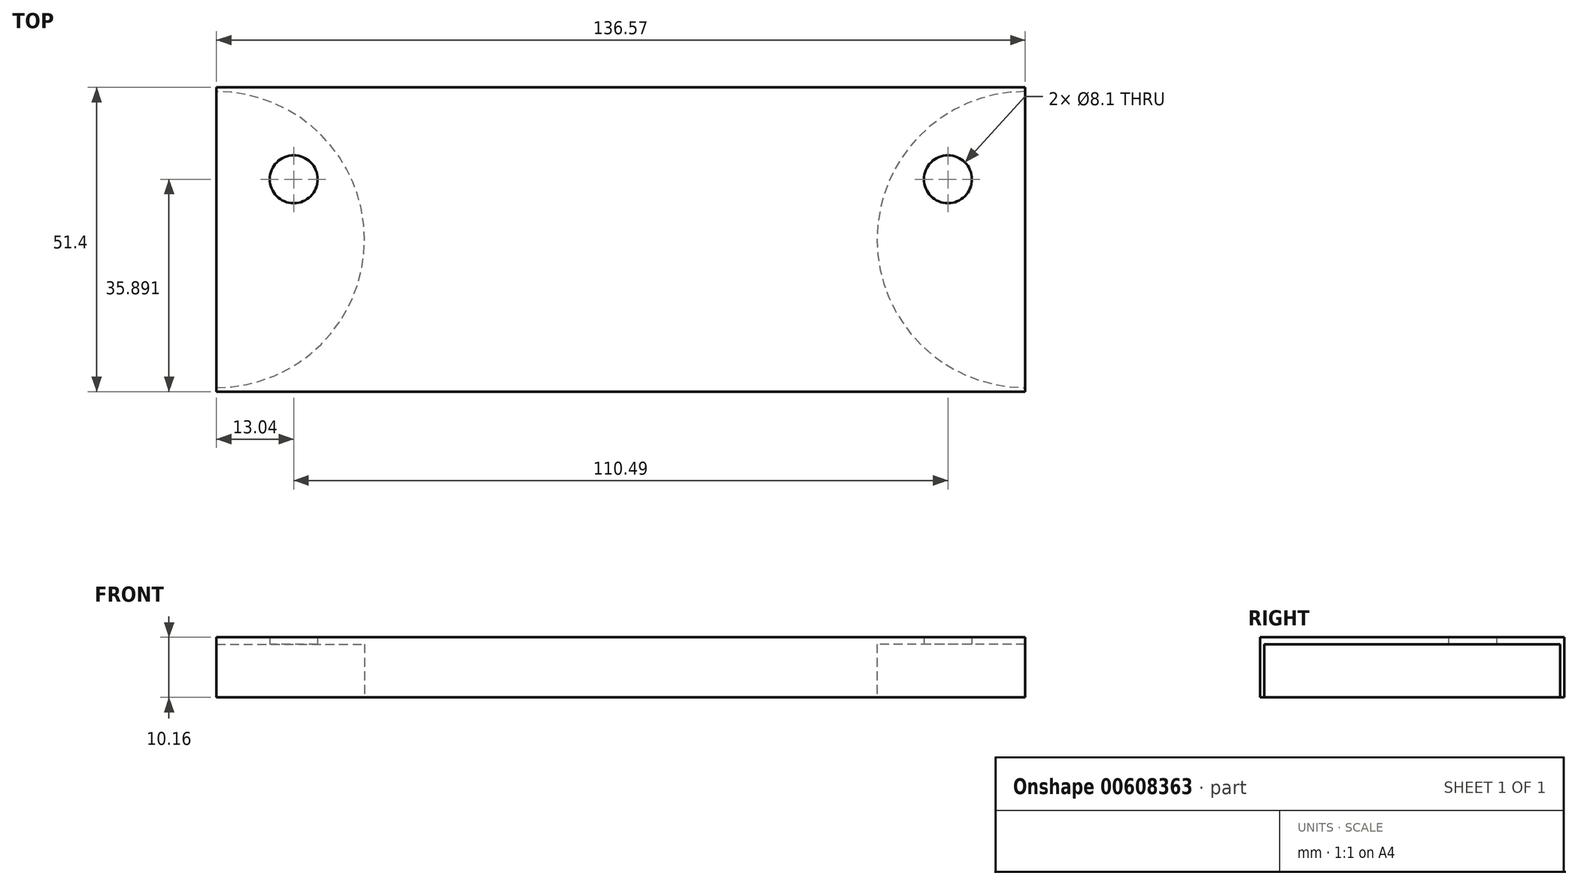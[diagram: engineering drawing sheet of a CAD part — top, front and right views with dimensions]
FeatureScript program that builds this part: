
annotation { "Feature Type Name" : "Feature", "Feature Type Description" : "" }
export const myFeature = defineFeature(function(context is Context, id is Id, definition is map)
    precondition{}
    {
        {
            var Q0;
            Q0=qCreatedBy(makeId("Top.planeOp"),FACE);
            var sketch = newSketch(context, id + "F0", { "sketchPlane" : qUnion([Q0])});
            skCircle(sketch, "E0", {"center": v(0, 0) * mm, "radius": 25.7 * mm});
            skCircle(sketch, "E1", {"center": v(13.04, 10.2) * mm, "radius": 4.05 * mm});
            skLineSegment(sketch, "E2", {"start": v(16.23, 12.69) * mm, "end": v(20.25, 15.83) * mm, "construction": true});
            skCircle(sketch, "E3", {"center": v(136.57, 0) * mm, "radius": 25.7 * mm});
            skCircle(sketch, "E4", {"center": v(123.53, 10.2) * mm, "radius": 4.05 * mm});
            skLineSegment(sketch, "E5", {"start": v(120.34, 12.69) * mm, "end": v(116.32, 15.83) * mm, "construction": true});
            skLineSegment(sketch, "E6", {"start": v(17.1, 10.2) * mm, "end": v(119.48, 10.2) * mm, "construction": true});
            skLineSegment(sketch, "E7", {"start": v(25.7, 0) * mm, "end": v(110.87, 0) * mm, "construction": true});
            skCircle(sketch, "E8", {"center": v(0, 0) * mm, "radius": 25 * mm});
            skCircle(sketch, "E9", {"center": v(136.57, 0) * mm, "radius": 25 * mm});
            skSolve(sketch);
        }
        {
            var Q0;
            Q0=makeQuery(id+"F0.imprint","IMPRINT",FACE,{"disambiguationData":[TD([[makeQuery(id+"F0.imprint","IMPRINT",EDGE,{"derivedFrom":sQuery(id+"F0.wireOp",EDGE,"E0")}),1.0]])]});
            var Q1;
            Q1=makeQuery(id+"F0.imprint","IMPRINT",FACE,{"disambiguationData":[TD([[makeQuery(id+"F0.imprint","IMPRINT",EDGE,{"derivedFrom":sQuery(id+"F0.wireOp",EDGE,"E1")}),-1.0]])]});
            var Q2;
            Q2=makeQuery(id+"F0.imprint","IMPRINT",FACE,{"disambiguationData":[TD([[makeQuery(id+"F0.imprint","IMPRINT",EDGE,{"derivedFrom":sQuery(id+"F0.wireOp",EDGE,"E3")}),1.0]])]});
            var Q3;
            Q3=makeQuery(id+"F0.imprint","IMPRINT",FACE,{"disambiguationData":[TD([[makeQuery(id+"F0.imprint","IMPRINT",EDGE,{"derivedFrom":sQuery(id+"F0.wireOp",EDGE,"E4")}),-1.0]])]});
            extrude(context, id + "F1", {"entities" : qUnion([Q0, Q1, Q2, Q3]), "depth" : 9.16 * mm, "offsetDistance" : 25 * mm});
        }
        {
            var Q0;
            Q0=qCreatedBy(makeId("Top.planeOp"),FACE);
            var sketch = newSketch(context, id + "F2", { "sketchPlane" : qUnion([Q0])});
            skCircle(sketch, "E10", {"center": v(13.04, 10.2) * mm, "radius": 4.05 * mm});
            skLineSegment(sketch, "E11", {"start": v(16.23, 12.69) * mm, "end": v(20.25, 15.83) * mm, "construction": true});
            skCircle(sketch, "E12", {"center": v(123.53, 10.2) * mm, "radius": 4.05 * mm});
            skLineSegment(sketch, "E13", {"start": v(120.34, 12.69) * mm, "end": v(116.32, 15.83) * mm, "construction": true});
            skLineSegment(sketch, "E14", {"start": v(17.1, 10.2) * mm, "end": v(119.48, 10.2) * mm, "construction": true});
            skCircle(sketch, "E15", {"center": v(0, 0) * mm, "radius": 25 * mm});
            skCircle(sketch, "E16", {"center": v(136.57, 0) * mm, "radius": 25 * mm});
            skSolve(sketch);
        }
        {
            var Q0;
            Q0=qCreatedBy(makeId("Top.planeOp"),FACE);
            var sketch = newSketch(context, id + "F3", { "sketchPlane" : qUnion([Q0])});
            skLineSegment(sketch, "E17.bottom", {"start": v(0, 25.7) * mm, "end": v(136.57, 25.7) * mm});
            skLineSegment(sketch, "E17.top", {"start": v(0, -25.7) * mm, "end": v(136.57, -25.7) * mm});
            skLineSegment(sketch, "E17.left", {"start": v(0, 25.7) * mm, "end": v(0, -25.7) * mm});
            skLineSegment(sketch, "E17.right", {"start": v(136.57, 25.7) * mm, "end": v(136.57, -25.7) * mm});
            skPoint(sketch, "E18.endSnap0", {"position": v(136.57, 0) * mm});
            skLineSegment(sketch, "E19", {"start": v(162.27, 0) * mm, "end": v(110.87, 0) * mm, "construction": true});
            skSolve(sketch);
        }
        {
            var Q0;
            Q0=qSketchRegion(id+"F3",true);
            extrude(context, id + "F4", {"entities" : qUnion([Q0]), "operationType" : NewBodyOperationType.ADD, "depth" : 9.16 * mm, "offsetDistance" : 25 * mm});
        }
        {
            var Q0;
            Q0=qSketchRegion(id+"F2",true);
            extrude(context, id + "F5", {"entities" : qUnion([Q0]), "operationType" : NewBodyOperationType.REMOVE, "depth" : 9 * mm, "offsetDistance" : 25 * mm});
        }
        {
            var Q0;
            Q0=makeQuery(id+"F5.boolean.opBoolean","SPLIT",FACE,{"disambiguationData":[TD([makeQuery(id+"F5.opExtrude","SWEPT_FACE",FACE,{"disambiguationData":[OSD([sQuery(id+"F2.wireOp",EDGE,"E12")])]})])],"derivedFrom":makeQuery(id+"F4.boolean.opBoolean","MERGE",FACE,{"derivedFrom":[makeQuery(id+"F1.opExtrude","CAP_FACE",FACE,{"disambiguationData":[OSD([sQuery(id+"F0.wireOp",EDGE,"E0"),sQuery(id+"F0.wireOp",EDGE,"E1")])],"isStart":true}),makeQuery(id+"F1.opExtrude","CAP_FACE",FACE,{"disambiguationData":[OSD([sQuery(id+"F0.wireOp",EDGE,"E3"),sQuery(id+"F0.wireOp",EDGE,"E4")])],"isStart":true}),makeQuery(id+"F4.opExtrude","CAP_FACE",FACE,{"disambiguationData":[OSD([sQuery(id+"F3.wireOp",EDGE,"E17.bottom"),sQuery(id+"F3.wireOp",EDGE,"E17.top"),sQuery(id+"F3.wireOp",EDGE,"E17.left"),sQuery(id+"F3.wireOp",EDGE,"E17.right")])],"isStart":true})]})});
            var Q1;
            Q1=makeQuery(id+"F5.boolean.opBoolean","SPLIT",FACE,{"disambiguationData":[TD([makeQuery(id+"F5.opExtrude","SWEPT_FACE",FACE,{"disambiguationData":[OSD([sQuery(id+"F2.wireOp",EDGE,"E10")])]})])],"derivedFrom":makeQuery(id+"F4.boolean.opBoolean","MERGE",FACE,{"derivedFrom":[makeQuery(id+"F1.opExtrude","CAP_FACE",FACE,{"disambiguationData":[OSD([sQuery(id+"F0.wireOp",EDGE,"E0"),sQuery(id+"F0.wireOp",EDGE,"E1")])],"isStart":true}),makeQuery(id+"F1.opExtrude","CAP_FACE",FACE,{"disambiguationData":[OSD([sQuery(id+"F0.wireOp",EDGE,"E3"),sQuery(id+"F0.wireOp",EDGE,"E4")])],"isStart":true}),makeQuery(id+"F4.opExtrude","CAP_FACE",FACE,{"disambiguationData":[OSD([sQuery(id+"F3.wireOp",EDGE,"E17.bottom"),sQuery(id+"F3.wireOp",EDGE,"E17.top"),sQuery(id+"F3.wireOp",EDGE,"E17.left"),sQuery(id+"F3.wireOp",EDGE,"E17.right")])],"isStart":true})]})});
            var Q2;
            Q2=sQuery(id+"F2.wireOp",EDGE,"E12");
            var Q3;
            Q3=sQuery(id+"F2.wireOp",EDGE,"E10");
            extrude(context, id + "F6", {"entities" : qUnion([Q0, Q1]), "operationType" : NewBodyOperationType.REMOVE, "surfaceEntities" : qUnion([Q2, Q3]), "oppositeDirection" : true, "depth" : 25 * mm, "offsetDistance" : 25 * mm});
        }
        {
            var Q0;
            Q0=qCreatedBy(makeId("Top.planeOp"),FACE);
            var sketch = newSketch(context, id + "F7", { "sketchPlane" : qUnion([Q0])});
            skLineSegment(sketch, "E20.left", {"start": v(162.27, 0) * mm, "end": v(162.27, 37.04) * mm, "construction": true});
            skLineSegment(sketch, "E20.right", {"start": v(-25.7, 0) * mm, "end": v(-25.7, 37.04) * mm, "construction": true});
            skLineSegment(sketch, "E21.left", {"start": v(162.27, 0) * mm, "end": v(162.27, -37.04) * mm, "construction": true});
            skLineSegment(sketch, "E21.right", {"start": v(-25.7, 0) * mm, "end": v(-25.7, -37.04) * mm, "construction": true});
            skLineSegment(sketch, "E22.bottom", {"start": v(162.27, 37.04) * mm, "end": v(136.57, 37.04) * mm});
            skLineSegment(sketch, "E22.top", {"start": v(162.27, -37.04) * mm, "end": v(136.57, -37.04) * mm});
            skLineSegment(sketch, "E22.left", {"start": v(162.27, 37.04) * mm, "end": v(162.27, -37.04) * mm});
            skLineSegment(sketch, "E22.right", {"start": v(136.57, 37.04) * mm, "end": v(136.57, -37.04) * mm});
            skLineSegment(sketch, "E23.bottom", {"start": v(-25.7, 37.04) * mm, "end": v(0, 37.04) * mm});
            skLineSegment(sketch, "E23.top", {"start": v(-25.7, -37.04) * mm, "end": v(0, -37.04) * mm});
            skLineSegment(sketch, "E23.left", {"start": v(-25.7, 37.04) * mm, "end": v(-25.7, -37.04) * mm});
            skLineSegment(sketch, "E23.right", {"start": v(0, 37.04) * mm, "end": v(0, -37.04) * mm});
            skLineSegment(sketch, "E24", {"start": v(162.27, 0) * mm, "end": v(-25.7, 0) * mm, "construction": true});
            skLineSegment(sketch, "E25", {"start": v(136.57, -25) * mm, "end": v(136.57, 25) * mm, "construction": true});
            skPoint(sketch, "E26", {"position": v(136.57, 0) * mm});
            skSolve(sketch);
        }
        {
            var Q0;
            Q0=makeQuery(id+"F7.imprint","IMPRINT",FACE,{"disambiguationData":[TD([[makeQuery(id+"F7.imprint","IMPRINT",EDGE,{"derivedFrom":sQuery(id+"F7.wireOp",EDGE,"E23.bottom")}),-1.0]])]});
            var Q1;
            Q1=makeQuery(id+"F7.imprint","IMPRINT",FACE,{"disambiguationData":[TD([[makeQuery(id+"F7.imprint","IMPRINT",EDGE,{"derivedFrom":sQuery(id+"F7.wireOp",EDGE,"E22.bottom")}),1.0]])]});
            extrude(context, id + "F8", {"entities" : qUnion([Q0, Q1]), "operationType" : NewBodyOperationType.REMOVE, "depth" : 25 * mm, "offsetDistance" : 25 * mm});
        }
        {
            var Q0;
            Q0=makeQuery(id+"F4.boolean.opBoolean","MERGE",FACE,{"derivedFrom":[makeQuery(id+"F1.opExtrude","CAP_FACE",FACE,{"disambiguationData":[OSD([sQuery(id+"F0.wireOp",EDGE,"E0"),sQuery(id+"F0.wireOp",EDGE,"E1")])],"isStart":false}),makeQuery(id+"F1.opExtrude","CAP_FACE",FACE,{"disambiguationData":[OSD([sQuery(id+"F0.wireOp",EDGE,"E3"),sQuery(id+"F0.wireOp",EDGE,"E4")])],"isStart":false}),makeQuery(id+"F4.opExtrude","CAP_FACE",FACE,{"disambiguationData":[OSD([sQuery(id+"F3.wireOp",EDGE,"E17.bottom"),sQuery(id+"F3.wireOp",EDGE,"E17.top"),sQuery(id+"F3.wireOp",EDGE,"E17.left"),sQuery(id+"F3.wireOp",EDGE,"E17.right")])],"isStart":false})]});
            extrude(context, id + "F9", {"entities" : qUnion([Q0]), "operationType" : NewBodyOperationType.ADD, "depth" : 1 * mm, "offsetDistance" : 25 * mm});
        }
    });
